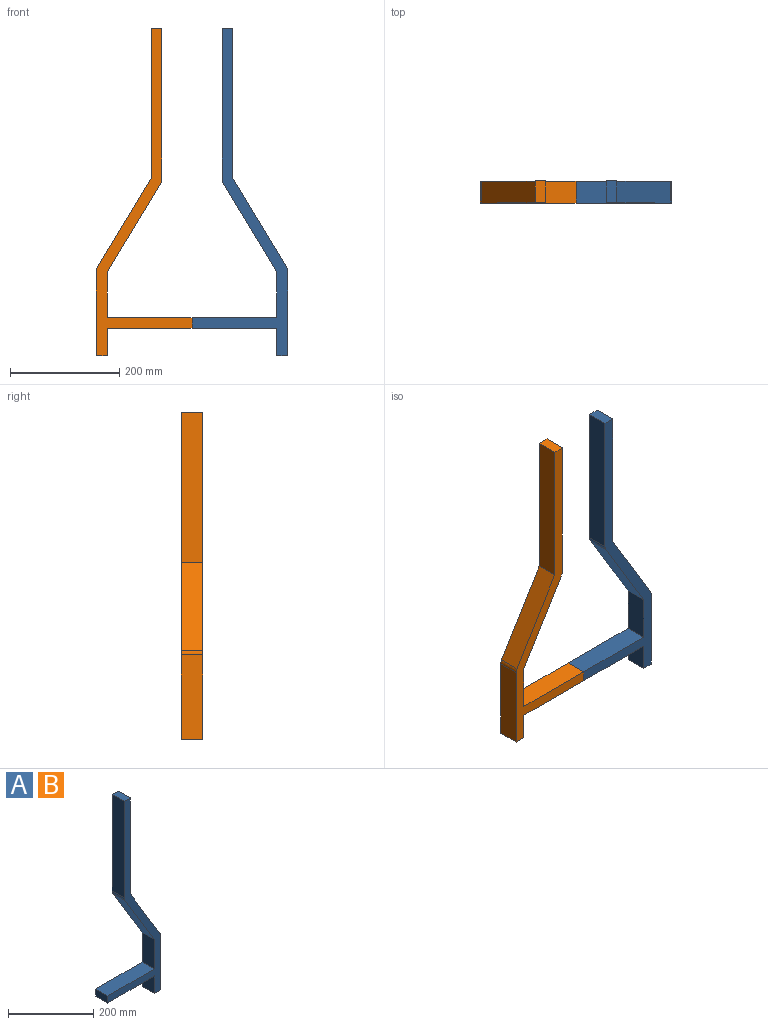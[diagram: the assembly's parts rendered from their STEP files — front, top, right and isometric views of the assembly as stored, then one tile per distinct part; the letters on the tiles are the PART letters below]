
ASSEMBLY  parts=2 mates=1
PART A: 16 faces, bbox 175x40x600 mm
  f0: plane 40x20mm, normal (0,0,-1), area 800mm2, adj f2,f3,f6,f13
  f1: plane 40x20mm, normal (0,0,1), area 800mm2, adj f2,f3,f5,f11
  f2: plane 600x175mm, normal (0,1,0), area 15655.2mm2, adj f0,f1,f4,f5,f6,f7,f8,f9
  f3: plane 600x175mm, normal (0,-1,0), area 15655.2mm2, adj f0,f1,f4,f5,f6,f7,f8,f9
  f4: plane 161.56x97.83mm, normal (-0.86,0,-0.52), area 7555mm2, adj f2,f3,f10,f15
  f5: plane 276.4x40mm, normal (-1,0,0), area 11055.8mm2, adj f1,f2,f3,f15
  f6: plane 50x40mm, normal (-1,0,0), area 2000mm2, adj f0,f2,f3,f7
  f7: plane 155x40mm, normal (0,0,-1), area 6200mm2, adj f2,f3,f6,f8
  f8: plane 40x20mm, normal (-1,0,0), area 800mm2, adj f2,f3,f7,f9
  f9: plane 155x40mm, normal (0,0,1), area 6200mm2, adj f2,f3,f8,f10
  f10: plane 84.27x40mm, normal (-1,0,0), area 3370.8mm2, adj f2,f3,f4,f9
  f11: plane 275x40mm, normal (1,0,0), area 11000mm2, adj f1,f2,f3,f12
  f12: plane 161.56x97.83mm, normal (0.86,0,0.52), area 7555mm2, adj f2,f3,f11,f14
  f13: plane 155.67x40mm, normal (1,0,0), area 6226.6mm2, adj f0,f2,f3,f14
  f14: cylinder r=15mm len=40mm, axis (0,-1,0), area 326.7mm2, adj f2,f3,f12,f13
  f15: cylinder r=15mm len=40mm, axis (0,-1,0), area 326.7mm2, adj f2,f3,f4,f5
PART B: same geometry as A
PLACE A t=(-289.47,-145.07,33.08)mm
PLACE B rot(axis=(0,0,1),180deg) t=(-289.47,-185.07,33.08)mm
MATE fastened B.f8 <-> A.f8  axis (1,0,0) through (-289.47,-165.07,-206.92)mm
